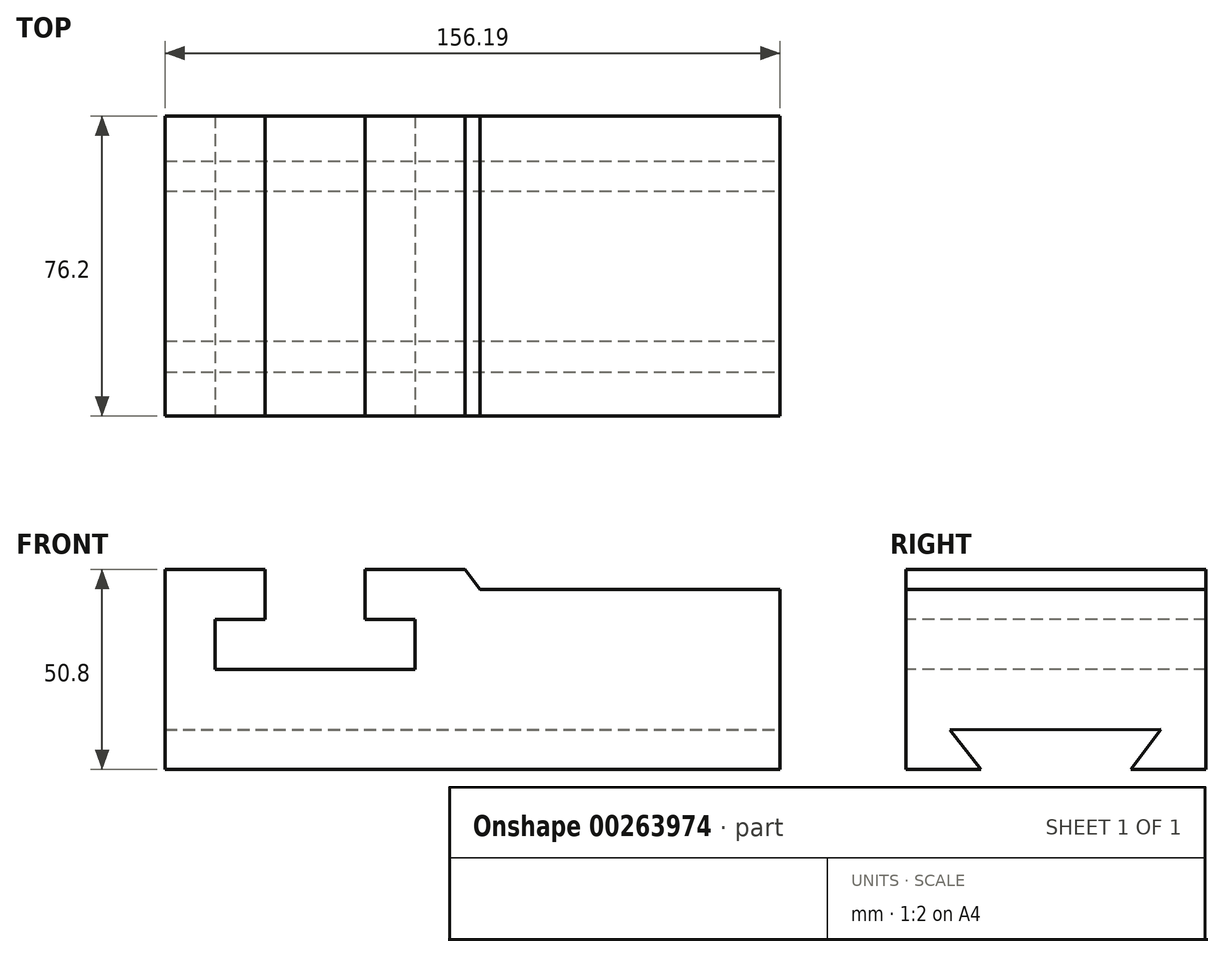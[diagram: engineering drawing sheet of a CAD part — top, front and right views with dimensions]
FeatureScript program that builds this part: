
annotation { "Feature Type Name" : "Feature", "Feature Type Description" : "" }
export const myFeature = defineFeature(function(context is Context, id is Id, definition is map)
    precondition{}
    {
        {
            var Q0;
            Q0=qCreatedBy(makeId("Front.planeOp"),FACE);
            var sketch = newSketch(context, id + "F0", { "sketchPlane" : qUnion([Q0])});
            skLineSegment(sketch, "E0", {"start": v(-76.2, 0) * mm, "end": v(-76.2, 50.8) * mm});
            skLineSegment(sketch, "E1", {"start": v(-76.2, 50.8) * mm, "end": v(-50.8, 50.8) * mm});
            skLineSegment(sketch, "E2", {"start": v(-50.8, 50.8) * mm, "end": v(-50.8, 38.1) * mm});
            skLineSegment(sketch, "E3", {"start": v(-50.8, 38.1) * mm, "end": v(-63.5, 38.1) * mm});
            skLineSegment(sketch, "E4", {"start": v(-63.5, 38.1) * mm, "end": v(-63.5, 25.4) * mm});
            skLineSegment(sketch, "E5", {"start": v(-63.5, 25.4) * mm, "end": v(-12.7, 25.4) * mm});
            skLineSegment(sketch, "E6", {"start": v(-12.7, 25.4) * mm, "end": v(-12.7, 38.1) * mm});
            skLineSegment(sketch, "E7", {"start": v(-12.7, 38.1) * mm, "end": v(-25.4, 38.1) * mm});
            skLineSegment(sketch, "E8", {"start": v(-25.4, 38.1) * mm, "end": v(-25.4, 50.8) * mm});
            skLineSegment(sketch, "E9", {"start": v(-25.4, 50.8) * mm, "end": v(0, 50.8) * mm});
            skLineSegment(sketch, "E10", {"start": v(0, 50.8) * mm, "end": v(3.8, 45.7) * mm});
            skLineSegment(sketch, "E11", {"start": v(3.8, 45.7) * mm, "end": v(80, 45.7) * mm});
            skLineSegment(sketch, "E12", {"start": v(80, 45.7) * mm, "end": v(80, 0) * mm});
            skLineSegment(sketch, "E13", {"start": v(80, 0) * mm, "end": v(-76.2, 0) * mm});
            skSolve(sketch);
        }
        {
            var Q0;
            Q0=makeQuery(id+"F0.imprint","IMPRINT",FACE,{"disambiguationData":[TD([[makeQuery(id+"F0.imprint","IMPRINT",EDGE,{"derivedFrom":sQuery(id+"F0.wireOp",EDGE,"E0")}),-1.0]])]});
            extrude(context, id + "F1", {"entities" : qUnion([Q0]), "oppositeDirection" : true, "depth" : 76.2 * mm});
        }
        {
            var Q0;
            Q0=makeQuery(id+"F1.opExtrude","SWEPT_FACE",FACE,{"disambiguationData":[OSD([sQuery(id+"F0.wireOp",EDGE,"E12")])]});
            var sketch = newSketch(context, id + "F2", { "sketchPlane" : qUnion([Q0])});
            skLineSegment(sketch, "E14", {"start": v(0, 0) * mm, "end": v(19.05, 0) * mm});
            skLineSegment(sketch, "E15", {"start": v(76.2, 0) * mm, "end": v(57.15, 0) * mm});
            skLineSegment(sketch, "E16", {"start": v(19.05, 0) * mm, "end": v(11.21, 10) * mm});
            skLineSegment(sketch, "E17", {"start": v(57.15, 0) * mm, "end": v(64.81, 10.13) * mm});
            skLineSegment(sketch, "E18", {"start": v(64.81, 10.13) * mm, "end": v(11.21, 10) * mm});
            skSolve(sketch);
        }
        {
            var Q0;
            {var subQ0=sQuery(id+"F2.wireOp",EDGE,"E16");Q0=makeQuery(id+"F2.imprint","IMPRINT",FACE,{"disambiguationData":[TD([[makeQuery(id+"F2.imprint","IMPRINT",EDGE,{"derivedFrom":subQ0}),-1.0]])]});}
            extrude(context, id + "F3", {"entities" : qUnion([Q0]), "operationType" : NewBodyOperationType.REMOVE, "endBound" : BoundingType.UP_TO_NEXT, "oppositeDirection" : true, "depth" : 25.4 * mm});
        }
    });
